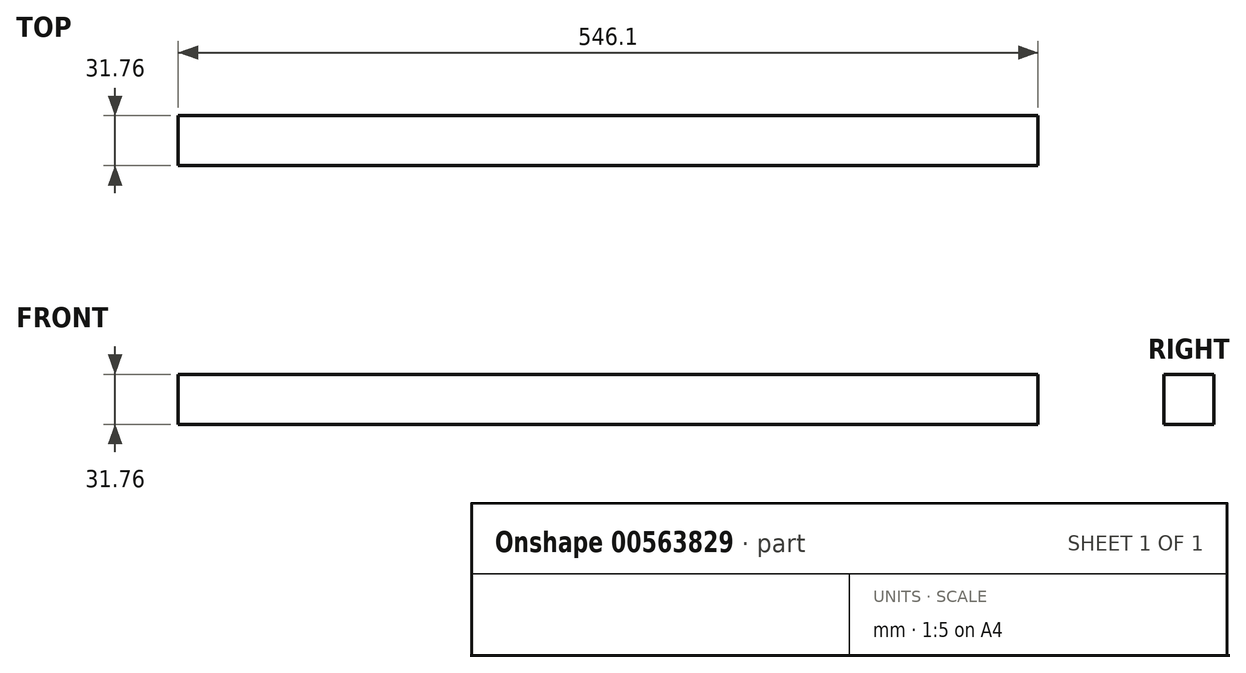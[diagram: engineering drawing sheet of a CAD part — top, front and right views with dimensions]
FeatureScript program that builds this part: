
annotation { "Feature Type Name" : "Feature", "Feature Type Description" : "" }
export const myFeature = defineFeature(function(context is Context, id is Id, definition is map)
    precondition{}
    {
        {
            var Q0;
            Q0=qCreatedBy(makeId("Front.planeOp"),FACE);
            var sketch = newSketch(context, id + "F0", { "sketchPlane" : qUnion([Q0])});
            skLineSegment(sketch, "E0.bottom", {"start": v(-273.05, 15.88) * mm, "end": v(273.05, 15.88) * mm});
            skLineSegment(sketch, "E0.top", {"start": v(-273.05, -15.88) * mm, "end": v(273.05, -15.88) * mm});
            skLineSegment(sketch, "E0.left", {"start": v(-273.05, 15.88) * mm, "end": v(-273.05, -15.88) * mm});
            skLineSegment(sketch, "E0.right", {"start": v(273.05, 15.88) * mm, "end": v(273.05, -15.88) * mm});
            skPoint(sketch, "E0.middle", {"position": v(0, 0) * mm});
            skSolve(sketch);
        }
        {
            var Q0;
            Q0=makeQuery(id+"F0.imprint","IMPRINT",FACE,{"disambiguationData":[TD([[makeQuery(id+"F0.imprint","IMPRINT",EDGE,{"derivedFrom":sQuery(id+"F0.wireOp",EDGE,"E0.bottom")}),-1.0]])]});
            extrude(context, id + "F1", {"entities" : qUnion([Q0]), "endBound" : BoundingType.SYMMETRIC, "depth" : 31.75 * mm, "offsetDistance" : 25.4 * mm});
        }
    });
